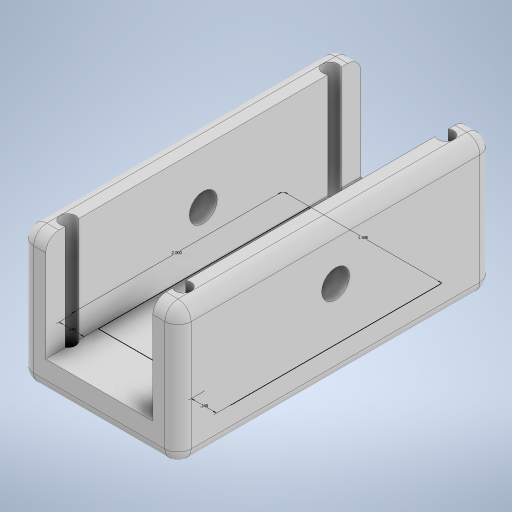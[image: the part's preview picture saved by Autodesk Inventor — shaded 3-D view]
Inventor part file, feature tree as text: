
AUTODESK INVENTOR PART (.ipt)
format: ipt  version: 2024.1 (Build 281209000, 209)  size: 348,672 bytes
history: native  units: in
note: dims shown in document units (in); Inventor stores cm internally (conversion verified against a paired STEP export)
features: extrude x5, sketch x5, hole x2, projected_geometry x2, fillet x1
ambient origin geometry x8: Origin, YZ Plane, XZ Plane, XY Plane, X Axis, Y Axis, Z Axis, Center Point
bodies: Solid1 (feature_tree)
feature tree (15):
  extrude  "Extrusion1"  Depth=1.5in
  extrude  "Extrusion2"  Depth=0.24in
  hole  "Hole1"  [1 undecoded]
  extrude  "Extrusion3"  Depth=0.125in TaperAngle=0.0deg
  extrude  "Extrusion4"  Depth=0.125in TaperAngle=0.0deg
  extrude  "Extrusion5"  Depth=0.62in
  sketch  "Sketch6"  dims[d8=0.5in]
  hole  "Hole2"  [1 undecoded]
  fillet  "Fillet1"  Radius=0.5in
  sketch  "Sketch3"  dims[d0=1.5in d1=2.0in]
  projected_geometry  "Projected Loop1"
  sketch  "Sketch4"  dims[d2=0.24in d3=0.24in]
  projected_geometry  "Projected Loop2"
  sketch  "Sketch5"  dims[d4=1.0in d5=0.0in d6=0.2in d7=0.0in]
  sketch  "Sketch7"  dims[d9=0.266in d10=0.75in d11=0.438in d12=0.25in d13=0.5635in d14=1.0in d15=0.8108in d16=0.5in d17=0.0in d18=0.5in d19=0.0in d20=0.62in d21=2.02in d22=0.5in d23=1.75in d24=0.5in d25=0.1in d26=0.0in d27=0.2in d28=0.25in d29=0.2in d30=0.25in d31=0.2in d32=0.25in d33=0.2in d34=0.1495in d35=0.75in d36=0.375in d37=0.25in d38=0.5635in d39=1.0in d40=0.8108in d41=0.125in]
note: 2 required parameter values undecoded (feature->parameter linkage not recoverable at this tier; creation-order binding heuristic only, values carry confidence <= 0.55)
